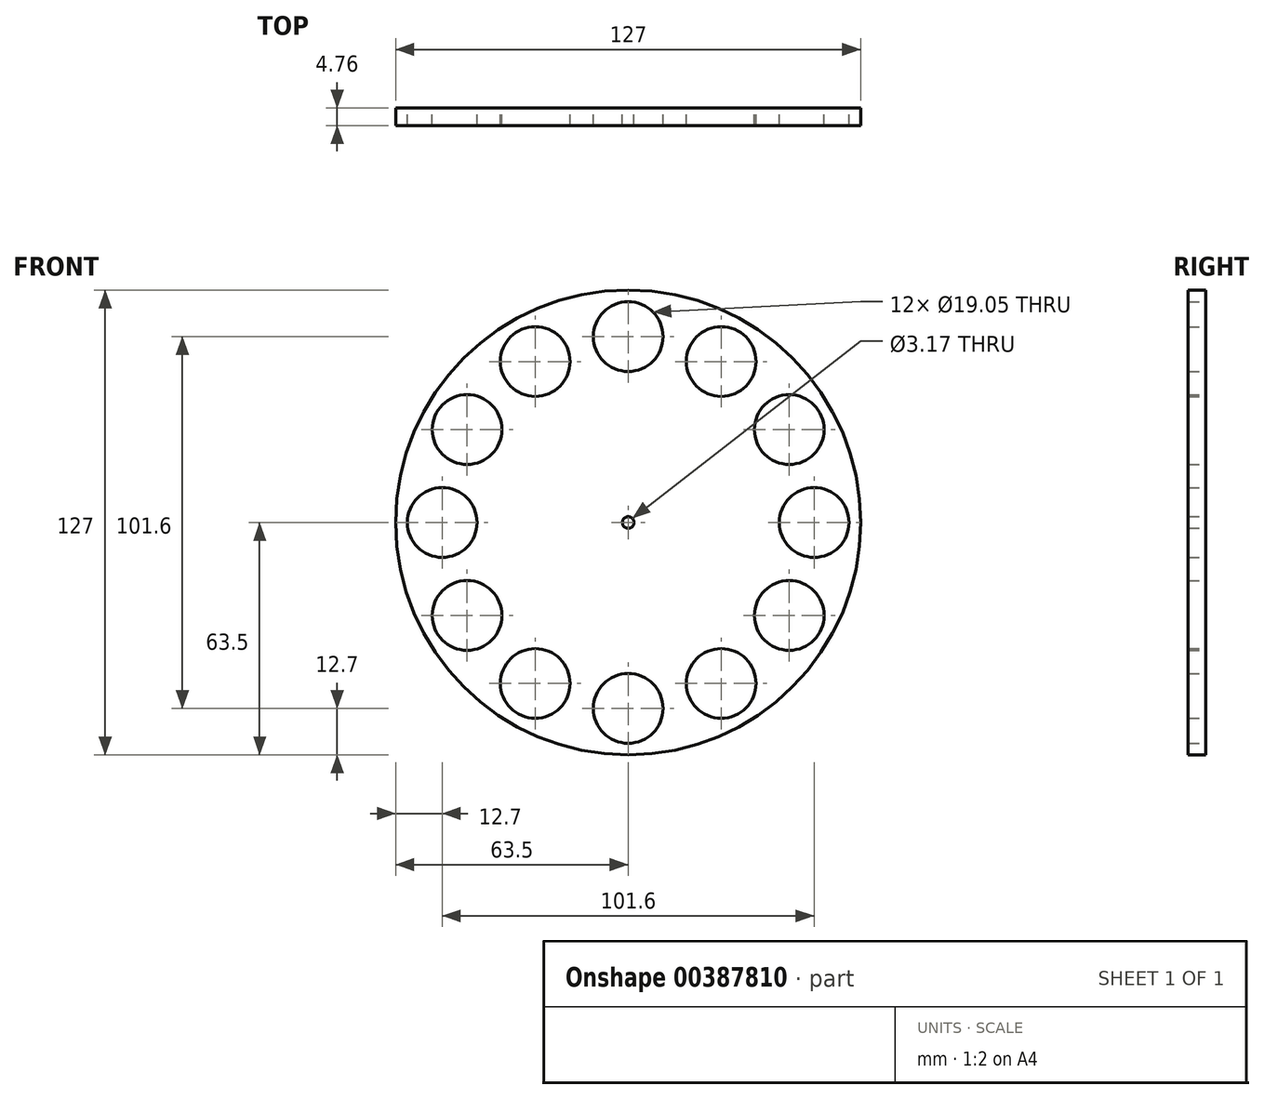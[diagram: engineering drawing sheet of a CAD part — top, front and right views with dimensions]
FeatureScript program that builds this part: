
annotation { "Feature Type Name" : "Feature", "Feature Type Description" : "" }
export const myFeature = defineFeature(function(context is Context, id is Id, definition is map)
    precondition{}
    {
        {
            var Q0;
            Q0=qCreatedBy(makeId("Front.planeOp"),FACE);
            var sketch = newSketch(context, id + "F0", { "sketchPlane" : qUnion([Q0])});
            skCircle(sketch, "E0", {"center": v(0, 0) * mm, "radius": 63.5 * mm});
            skCircle(sketch, "E1", {"center": v(0, 50.8) * mm, "radius": 9.53 * mm});
            skCircle(sketch, "E2", {"center": v(0, 0) * mm, "radius": 50.8 * mm, "construction": true});
            skCircle(sketch, "E3.1.0", {"center": v(-25.4, 44) * mm, "radius": 9.53 * mm});
            skCircle(sketch, "E3.2.0", {"center": v(-44, 25.4) * mm, "radius": 9.53 * mm});
            skCircle(sketch, "E3.3.0", {"center": v(-50.8, 0) * mm, "radius": 9.53 * mm});
            skCircle(sketch, "E3.4.0", {"center": v(-44, -25.4) * mm, "radius": 9.53 * mm});
            skCircle(sketch, "E3.5.0", {"center": v(-25.4, -44) * mm, "radius": 9.53 * mm});
            skCircle(sketch, "E3.6.0", {"center": v(0, -50.8) * mm, "radius": 9.52 * mm});
            skCircle(sketch, "E3.7.0", {"center": v(25.4, -44) * mm, "radius": 9.53 * mm});
            skCircle(sketch, "E3.8.0", {"center": v(44, -25.4) * mm, "radius": 9.53 * mm});
            skCircle(sketch, "E3.9.0", {"center": v(50.8, 0) * mm, "radius": 9.53 * mm});
            skCircle(sketch, "E4", {"center": v(0, 0) * mm, "radius": 1.59 * mm});
            skCircle(sketch, "E5.1.10.0", {"center": v(44, 25.4) * mm, "radius": 9.53 * mm});
            skCircle(sketch, "E5.1.11.0", {"center": v(25.4, 44) * mm, "radius": 9.53 * mm});
            skSolve(sketch);
        }
        {
            var Q0;
            Q0 = qSketchRegion(id + "F0", true);
            extrude(context, id + "F1", {"entities" : qUnion([Q0]), "depth" : 4.76 * mm, "offsetDistance" : 25.4 * mm});
        }
    });
